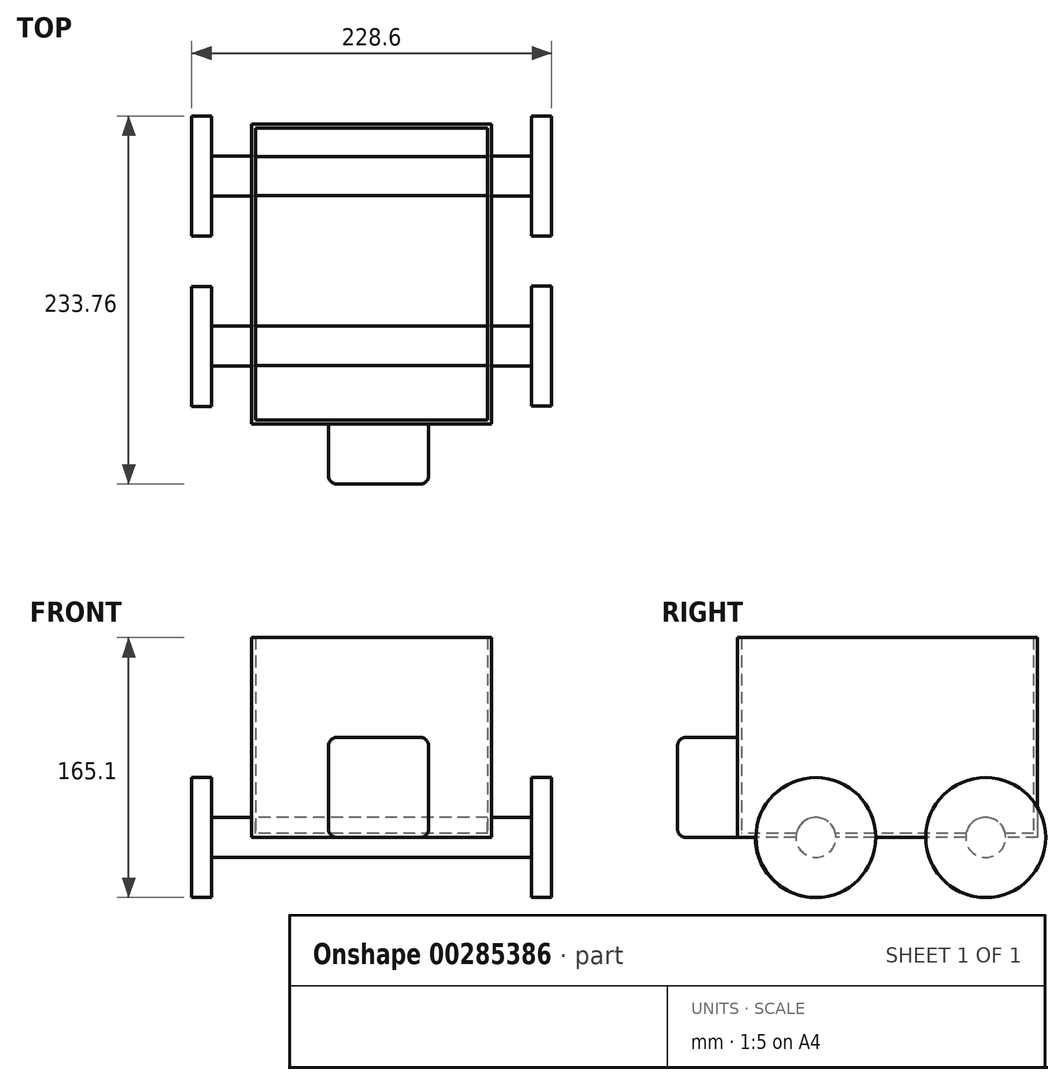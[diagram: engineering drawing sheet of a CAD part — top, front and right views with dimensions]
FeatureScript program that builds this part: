
annotation { "Feature Type Name" : "Feature", "Feature Type Description" : "" }
export const myFeature = defineFeature(function(context is Context, id is Id, definition is map)
    precondition{}
    {
        {
            var Q0;
            Q0=qCreatedBy(makeId("Top.planeOp"),FACE);
            var sketch = newSketch(context, id + "F0", { "sketchPlane" : qUnion([Q0])});
            skLineSegment(sketch, "E0.bottom", {"start": v(-77.5, 107.23) * mm, "end": v(74.9, 107.23) * mm});
            skLineSegment(sketch, "E0.top", {"start": v(-77.5, -83.27) * mm, "end": v(74.9, -83.27) * mm});
            skLineSegment(sketch, "E0.left", {"start": v(-77.5, 107.23) * mm, "end": v(-77.5, -83.27) * mm});
            skLineSegment(sketch, "E0.right", {"start": v(74.9, 107.23) * mm, "end": v(74.9, -83.27) * mm});
            skSolve(sketch);
        }
        {
            var Q0;
            Q0=makeQuery(id+"F0.imprint","IMPRINT",FACE,{"disambiguationData":[TD([[makeQuery(id+"F0.imprint","IMPRINT",EDGE,{"derivedFrom":sQuery(id+"F0.wireOp",EDGE,"E0.bottom")}),-1.0]])]});
            extrude(context, id + "F1", {"entities" : qUnion([Q0]), "depth" : 127 * mm});
        }
        {
            var Q0;
            Q0=makeQuery(id+"F1.opExtrude","CAP_FACE",FACE,{"disambiguationData":[OSD([sQuery(id+"F0.wireOp",EDGE,"E0.bottom"),sQuery(id+"F0.wireOp",EDGE,"E0.top"),sQuery(id+"F0.wireOp",EDGE,"E0.left"),sQuery(id+"F0.wireOp",EDGE,"E0.right")])],"isStart":false});
            shell(context, id + "F2", {"entities" : qUnion([Q0]), "thickness" : 2.54 * mm});
        }
        {
            var Q0;
            Q0=makeQuery(id+"F1.opExtrude","SWEPT_FACE",FACE,{"disambiguationData":[OSD([sQuery(id+"F0.wireOp",EDGE,"E0.top")])]});
            var sketch = newSketch(context, id + "F3", { "sketchPlane" : qUnion([Q0])});
            skLineSegment(sketch, "E1.bottom", {"start": v(-28.66, 0) * mm, "end": v(34.84, 0) * mm});
            skLineSegment(sketch, "E1.top", {"start": v(-28.66, 63.5) * mm, "end": v(34.84, 63.5) * mm});
            skLineSegment(sketch, "E1.left", {"start": v(-28.66, 0) * mm, "end": v(-28.66, 63.5) * mm});
            skLineSegment(sketch, "E1.right", {"start": v(34.84, 0) * mm, "end": v(34.84, 63.5) * mm});
            skSolve(sketch);
        }
        {
            var Q0;
            Q0=makeQuery(id+"F3.imprint","IMPRINT",FACE,{"disambiguationData":[TD([[makeQuery(id+"F3.imprint","IMPRINT",EDGE,{"derivedFrom":sQuery(id+"F3.wireOp",EDGE,"E1.bottom")}),1.0]])]});
            extrude(context, id + "F4", {"entities" : qUnion([Q0]), "operationType" : NewBodyOperationType.ADD, "depth" : 38.1 * mm});
        }
        {
            var Q0;
            Q0=makeQuery(id+"F4.opExtrude","CAP_EDGE",EDGE,{"disambiguationData":[OSD([sQuery(id+"F3.wireOp",EDGE,"E1.left")])],"isStart":false});
            var Q1;
            Q1=makeQuery(id+"F4.opExtrude","CAP_EDGE",EDGE,{"disambiguationData":[OSD([sQuery(id+"F3.wireOp",EDGE,"E1.right")])],"isStart":false});
            var Q2;
            Q2=makeQuery(id+"F4.opExtrude","CAP_EDGE",EDGE,{"disambiguationData":[OSD([sQuery(id+"F3.wireOp",EDGE,"E1.top")])],"isStart":false});
            var Q3;
            Q3=makeQuery(id+"F4.opExtrude","SWEPT_EDGE",EDGE,{"disambiguationData":[OSD([sQuery(id+"F3.wireOp",EDGE,"E1.top"),sQuery(id+"F3.wireOp",EDGE,"E1.right")])]});
            var Q4;
            Q4=makeQuery(id+"F4.opExtrude","SWEPT_EDGE",EDGE,{"disambiguationData":[OSD([sQuery(id+"F3.wireOp",EDGE,"E1.top"),sQuery(id+"F3.wireOp",EDGE,"E1.left")])]});
            var Q5;
            Q5=makeQuery(id+"F4.opExtrude","CAP_EDGE",EDGE,{"disambiguationData":[OSD([sQuery(id+"F3.wireOp",EDGE,"E1.bottom")])],"isStart":false});
            var Q6;
            Q6=makeQuery(id+"F4.opExtrude","SWEPT_EDGE",EDGE,{"disambiguationData":[OSD([sQuery(id+"F0.wireOp",EDGE,"E0.top"),sQuery(id+"F3.wireOp",EDGE,"E1.bottom"),sQuery(id+"F3.wireOp",EDGE,"E1.left")])]});
            var Q7;
            Q7=makeQuery(id+"F4.opExtrude","SWEPT_EDGE",EDGE,{"disambiguationData":[OSD([sQuery(id+"F0.wireOp",EDGE,"E0.top"),sQuery(id+"F3.wireOp",EDGE,"E1.bottom"),sQuery(id+"F3.wireOp",EDGE,"E1.right")])]});
            fillet(context, id + "F5", {"entities" : qUnion([Q0, Q1, Q2, Q3, Q4, Q5, Q6, Q7]), "radius" : 5.08 * mm, "tangentPropagation" : true, "allowEdgeOverflow" : false});
        }
        {
            var Q0;
            Q0=makeQuery(id+"F1.opExtrude","SWEPT_FACE",FACE,{"disambiguationData":[OSD([sQuery(id+"F0.wireOp",EDGE,"E0.left")])]});
            var sketch = newSketch(context, id + "F6", { "sketchPlane" : qUnion([Q0])});
            skCircle(sketch, "E2", {"center": v(33.55, 0) * mm, "radius": 12.7 * mm});
            skCircle(sketch, "E3", {"center": v(-74.28, 0) * mm, "radius": 12.7 * mm});
            skSolve(sketch);
        }
        {
            var Q0;
            {var subQ0=sQuery(id+"F6.wireOp",EDGE,"E2");var subQ1=makeQuery(id+"F1.opExtrude","CAP_EDGE",EDGE,{"disambiguationData":[OSD([sQuery(id+"F0.wireOp",EDGE,"E0.left")])],"isStart":true});var subQ2=makeQuery(id+"F6.imprint","INTERSECT",VERTEX,{"disambiguationData":[OD(0.0)],"derivedFrom":[subQ1,subQ0]});Q0=makeQuery(id+"F6.imprint","IMPRINT",FACE,{"disambiguationData":[TD([[makeQuery(id+"F6.imprint","IMPRINT",EDGE,{"disambiguationData":[TD([[subQ2,1.0]])],"derivedFrom":subQ0}),1.0]])]});}
            var Q1;
            {var subQ0=sQuery(id+"F6.wireOp",EDGE,"E3");var subQ1=makeQuery(id+"F1.opExtrude","CAP_EDGE",EDGE,{"disambiguationData":[OSD([sQuery(id+"F0.wireOp",EDGE,"E0.left")])],"isStart":true});var subQ2=makeQuery(id+"F6.imprint","INTERSECT",VERTEX,{"disambiguationData":[OD(0.0)],"derivedFrom":[subQ1,subQ0]});Q1=makeQuery(id+"F6.imprint","IMPRINT",FACE,{"disambiguationData":[TD([[makeQuery(id+"F6.imprint","IMPRINT",EDGE,{"disambiguationData":[TD([[subQ2,-1.0]])],"derivedFrom":subQ0}),1.0]])]});}
            var Q2;
            {var subQ0=sQuery(id+"F6.wireOp",EDGE,"E2");var subQ1=makeQuery(id+"F1.opExtrude","CAP_EDGE",EDGE,{"disambiguationData":[OSD([sQuery(id+"F0.wireOp",EDGE,"E0.left")])],"isStart":true});var subQ2=makeQuery(id+"F6.imprint","INTERSECT",VERTEX,{"disambiguationData":[OD(0.0)],"derivedFrom":[subQ1,subQ0]});Q2=makeQuery(id+"F6.imprint","IMPRINT",FACE,{"disambiguationData":[TD([[makeQuery(id+"F6.imprint","IMPRINT",EDGE,{"disambiguationData":[TD([[subQ2,-1.0]])],"derivedFrom":subQ0}),1.0]])]});}
            var Q3;
            {var subQ0=sQuery(id+"F6.wireOp",EDGE,"E3");var subQ1=makeQuery(id+"F1.opExtrude","CAP_EDGE",EDGE,{"disambiguationData":[OSD([sQuery(id+"F0.wireOp",EDGE,"E0.left")])],"isStart":true});var subQ2=makeQuery(id+"F6.imprint","INTERSECT",VERTEX,{"disambiguationData":[OD(0.0)],"derivedFrom":[subQ1,subQ0]});Q3=makeQuery(id+"F6.imprint","IMPRINT",FACE,{"disambiguationData":[TD([[makeQuery(id+"F6.imprint","IMPRINT",EDGE,{"disambiguationData":[TD([[subQ2,1.0]])],"derivedFrom":subQ0}),1.0]])]});}
            extrude(context, id + "F7", {"entities" : qUnion([Q0, Q1, Q2, Q3]), "operationType" : NewBodyOperationType.ADD, "oppositeDirection" : true, "depth" : 177.8 * mm});
        }
        {
            var Q0;
            Q0=makeQuery(id+"F7.opExtrude","CAP_FACE",FACE,{"disambiguationData":[OSD([sQuery(id+"F6.wireOp",EDGE,"E2")])],"isStart":false});
            var sketch = newSketch(context, id + "F8", { "sketchPlane" : qUnion([Q0])});
            skCircle(sketch, "E4", {"center": v(-33.55, 0) * mm, "radius": 38.1 * mm});
            skCircle(sketch, "E5", {"center": v(74.3, 0) * mm, "radius": 38.1 * mm});
            skSolve(sketch);
        }
        {
            var Q0;
            Q0 = qSketchRegion(id + "F8", true);
            extrude(context, id + "F9", {"entities" : qUnion([Q0]), "operationType" : NewBodyOperationType.ADD, "depth" : 12.7 * mm});
        }
        {
            var Q0;
            Q0=makeQuery(id+"F7.boolean.opBoolean","MERGE",FACE,{"derivedFrom":[makeQuery(id+"F1.opExtrude","SWEPT_FACE",FACE,{"disambiguationData":[OSD([sQuery(id+"F0.wireOp",EDGE,"E0.left")])]}),makeQuery(id+"F7.opExtrude","CAP_FACE",FACE,{"disambiguationData":[OSD([sQuery(id+"F6.wireOp",EDGE,"E2")])],"isStart":true}),makeQuery(id+"F7.opExtrude","CAP_FACE",FACE,{"disambiguationData":[OSD([sQuery(id+"F6.wireOp",EDGE,"E3")])],"isStart":true})]});
            var sketch = newSketch(context, id + "F10", { "sketchPlane" : qUnion([Q0])});
            skCircle(sketch, "E6", {"center": v(-74.28, 0) * mm, "radius": 12.7 * mm});
            skCircle(sketch, "E7", {"center": v(33.55, 0) * mm, "radius": 12.7 * mm});
            skSolve(sketch);
        }
        {
            var Q0;
            {var subQ0=sQuery(id+"F10.wireOp",EDGE,"E7");var subQ1=makeQuery(id+"F4.opExtrude","SWEPT_FACE",FACE,{"disambiguationData":[OSD([sQuery(id+"F3.wireOp",EDGE,"E1.bottom")])]});var subQ2=sQuery(id+"F0.wireOp",EDGE,"E0.left");var subQ3=makeQuery(id+"F1.opExtrude","SWEPT_FACE",FACE,{"disambiguationData":[OSD([subQ2])]});var subQ4=sQuery(id+"F6.wireOp",EDGE,"E2");var subQ5=makeQuery(id+"F7.opExtrude","CAP_FACE",FACE,{"disambiguationData":[OSD([subQ4])],"isStart":true});var subQ6=sQuery(id+"F0.wireOp",EDGE,"E0.top");var subQ7=makeQuery(id+"F7.opExtrude","SWEPT_FACE",FACE,{"disambiguationData":[OSD([subQ4])]});var subQ8=makeQuery(id+"F1.opExtrude","CAP_FACE",FACE,{"disambiguationData":[OSD([sQuery(id+"F0.wireOp",EDGE,"E0.bottom"),subQ6,subQ2,sQuery(id+"F0.wireOp",EDGE,"E0.right")])],"isStart":true});var subQ9=sQuery(id+"F6.wireOp",EDGE,"E3");var subQ10=makeQuery(id+"F7.opExtrude","CAP_FACE",FACE,{"disambiguationData":[OSD([subQ9])],"isStart":true});var subQ11=makeQuery(id+"F1.opExtrude","CAP_EDGE",EDGE,{"disambiguationData":[OSD([subQ2])],"isStart":true});var subQ12=makeQuery(id+"F10.imprint","INTERSECT",VERTEX,{"derivedFrom":[makeQuery(id+"F7.boolean.opBoolean","SPLIT",EDGE,{"disambiguationData":[TD([subQ8,makeQuery(id+"F1.opExtrude","SWEPT_FACE",FACE,{"disambiguationData":[OSD([subQ6])]}),subQ3,subQ1,subQ7,subQ5,subQ10])],"derivedFrom":subQ11}),subQ0]});Q0=makeQuery(id+"F10.imprint","IMPRINT",FACE,{"disambiguationData":[TD([[makeQuery(id+"F10.imprint","IMPRINT",EDGE,{"disambiguationData":[TD([[subQ12,-1.0]])],"derivedFrom":subQ0}),1.0]])]});}
            var Q1;
            {var subQ0=sQuery(id+"F10.wireOp",EDGE,"E6");var subQ1=makeQuery(id+"F4.opExtrude","SWEPT_FACE",FACE,{"disambiguationData":[OSD([sQuery(id+"F3.wireOp",EDGE,"E1.bottom")])]});var subQ2=sQuery(id+"F0.wireOp",EDGE,"E0.left");var subQ3=makeQuery(id+"F1.opExtrude","SWEPT_FACE",FACE,{"disambiguationData":[OSD([subQ2])]});var subQ4=sQuery(id+"F6.wireOp",EDGE,"E2");var subQ5=makeQuery(id+"F7.opExtrude","CAP_FACE",FACE,{"disambiguationData":[OSD([subQ4])],"isStart":true});var subQ6=sQuery(id+"F0.wireOp",EDGE,"E0.bottom");var subQ7=makeQuery(id+"F1.opExtrude","CAP_FACE",FACE,{"disambiguationData":[OSD([subQ6,sQuery(id+"F0.wireOp",EDGE,"E0.top"),subQ2,sQuery(id+"F0.wireOp",EDGE,"E0.right")])],"isStart":true});var subQ8=sQuery(id+"F6.wireOp",EDGE,"E3");var subQ9=makeQuery(id+"F7.opExtrude","SWEPT_FACE",FACE,{"disambiguationData":[OSD([subQ8])]});var subQ10=makeQuery(id+"F7.opExtrude","CAP_FACE",FACE,{"disambiguationData":[OSD([subQ8])],"isStart":true});var subQ11=makeQuery(id+"F1.opExtrude","CAP_EDGE",EDGE,{"disambiguationData":[OSD([subQ2])],"isStart":true});var subQ12=makeQuery(id+"F10.imprint","INTERSECT",VERTEX,{"derivedFrom":[makeQuery(id+"F7.boolean.opBoolean","SPLIT",EDGE,{"disambiguationData":[TD([makeQuery(id+"F1.opExtrude","SWEPT_FACE",FACE,{"disambiguationData":[OSD([subQ6])]}),subQ7,subQ3,subQ1,subQ5,subQ9,subQ10])],"derivedFrom":subQ11}),subQ0]});Q1=makeQuery(id+"F10.imprint","IMPRINT",FACE,{"disambiguationData":[TD([[makeQuery(id+"F10.imprint","IMPRINT",EDGE,{"disambiguationData":[TD([[subQ12,1.0]])],"derivedFrom":subQ0}),1.0]])]});}
            extrude(context, id + "F11", {"entities" : qUnion([Q0, Q1]), "operationType" : NewBodyOperationType.ADD, "depth" : 25.4 * mm});
        }
        {
            var Q0;
            Q0=makeQuery(id+"F11.opExtrude","CAP_FACE",FACE,{"disambiguationData":[OSD([sQuery(id+"F10.wireOp",EDGE,"E6")])],"isStart":false});
            var sketch = newSketch(context, id + "F12", { "sketchPlane" : qUnion([Q0])});
            skCircle(sketch, "E8", {"center": v(-74.28, 0) * mm, "radius": 38.1 * mm});
            skCircle(sketch, "E9", {"center": v(33.97, 0) * mm, "radius": 38.1 * mm});
            skSolve(sketch);
        }
        {
            var Q0;
            Q0=makeQuery(id+"F12.imprint","IMPRINT",FACE,{"disambiguationData":[TD([[makeQuery(id+"F12.imprint","IMPRINT",EDGE,{"derivedFrom":sQuery(id+"F12.wireOp",EDGE,"E9")}),1.0]])]});
            var Q1;
            Q1=makeQuery(id+"F12.imprint","IMPRINT",FACE,{"disambiguationData":[TD([[makeQuery(id+"F12.imprint","IMPRINT",EDGE,{"derivedFrom":makeQuery(id+"F11.opExtrude","CAP_EDGE",EDGE,{"disambiguationData":[OSD([sQuery(id+"F10.wireOp",EDGE,"E6")])],"isStart":false})}),1.0]])]});
            var Q2;
            Q2=makeQuery(id+"F12.imprint","IMPRINT",FACE,{"disambiguationData":[TD([[makeQuery(id+"F12.imprint","IMPRINT",EDGE,{"derivedFrom":sQuery(id+"F12.wireOp",EDGE,"E8")}),1.0]])]});
            extrude(context, id + "F13", {"entities" : qUnion([Q0, Q1, Q2]), "operationType" : NewBodyOperationType.ADD, "depth" : 12.7 * mm});
        }
    });
